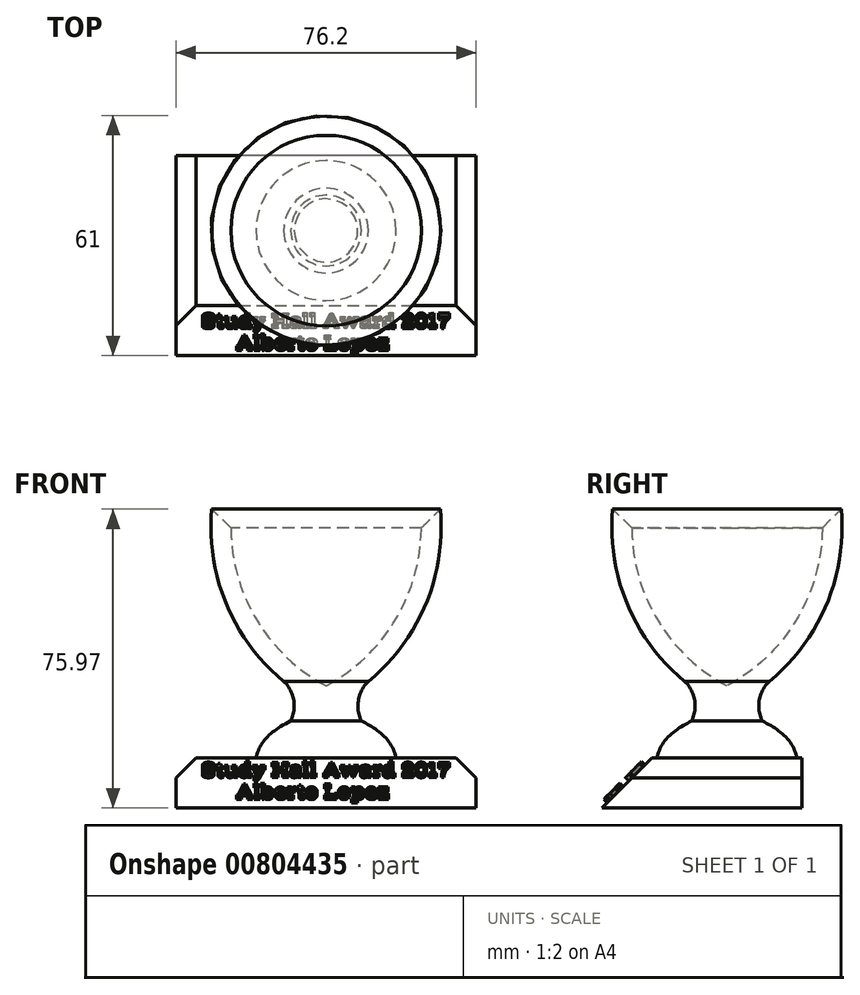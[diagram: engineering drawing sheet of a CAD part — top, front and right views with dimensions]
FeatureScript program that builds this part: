
annotation { "Feature Type Name" : "Feature", "Feature Type Description" : "" }
export const myFeature = defineFeature(function(context is Context, id is Id, definition is map)
    precondition{}
    {
        {
            var Q0;
            Q0=qCreatedBy(makeId("Top.planeOp"),FACE);
            var sketch = newSketch(context, id + "F0", { "sketchPlane" : qUnion([Q0])});
            skLineSegment(sketch, "E0.bottom", {"start": v(38.1, 25.4) * mm, "end": v(-38.1, 25.4) * mm});
            skLineSegment(sketch, "E0.top", {"start": v(38.1, -25.4) * mm, "end": v(-38.1, -25.4) * mm});
            skLineSegment(sketch, "E0.left", {"start": v(38.1, 25.4) * mm, "end": v(38.1, -25.4) * mm});
            skLineSegment(sketch, "E0.right", {"start": v(-38.1, 25.4) * mm, "end": v(-38.1, -25.4) * mm});
            skPoint(sketch, "E0.middle", {"position": v(0, 0) * mm});
            skSolve(sketch);
        }
        {
            var Q0;
            Q0=makeQuery(id+"F0.imprint","IMPRINT",FACE,{"disambiguationData":[TD([[makeQuery(id+"F0.imprint","IMPRINT",EDGE,{"derivedFrom":sQuery(id+"F0.wireOp",EDGE,"E0.bottom")}),1.0]])]});
            extrude(context, id + "F1", {"entities" : qUnion([Q0]), "depth" : 12.7 * mm, "offsetDistance" : 25.4 * mm});
        }
        {
            var Q0;
            Q0=makeQuery(id+"F1.opExtrude","CAP_EDGE",EDGE,{"disambiguationData":[OSD([sQuery(id+"F0.wireOp",EDGE,"E0.top")])],"isStart":false});
            chamfer(context, id + "F2", {"entities" : qUnion([Q0]), "width" : 12.7 * mm, "tangentPropagation" : true});
        }
        {
            var Q0;
            Q0=makeQuery(id+"F2.opChamfer","BLEND_FACE",FACE,{"disambiguationData":[OSD([sQuery(id+"F0.wireOp",EDGE,"E0.top")])]});
            var sketch = newSketch(context, id + "F3", { "sketchPlane" : qUnion([Q0])});
            skText(sketch, "E1", { "text": "Study Hall Award 2017\n      Alberto Lopez", "fontName": "RobotoSlab-Regular.ttf"});
            const initialGuessF3  = {"E1": [-0.03175, -0.007, 1, 0, 0.00428]};
            skSetInitialGuess(sketch, initialGuessF3);
            skSolve(sketch);
        }
        {
            var Q0;
            Q0=qSketchRegion(id+"F3",true);
            extrude(context, id + "F4", {"entities" : qUnion([Q0]), "operationType" : NewBodyOperationType.ADD, "depth" : 1.27 * mm, "offsetDistance" : 25.4 * mm});
        }
        {
            var Q0;
            Q0=qCreatedBy(makeId("Front.planeOp"),FACE);
            cPlane(context, id + "F5", {"entities" : qUnion([Q0]), "cplaneType" : CPlaneType.OFFSET, "offset" : 6.35 * mm, "oppositeDirection" : true, "width" : 152.4 * mm, "height" : 152.4 * mm});
        }
        {
            var Q0;
            Q0=qCreatedBy(id+"F5.planeOp",FACE);
            var sketch = newSketch(context, id + "F6", { "sketchPlane" : qUnion([Q0])});
            skLineSegment(sketch, "E2", {"start": v(0, 0) * mm, "end": v(0, 76.2) * mm});
            skLineSegment(sketch, "E3", {"start": v(0, 76.2) * mm, "end": v(29.02, 76.2) * mm});
            skArc(sketch, "E4", {"start": v(0, 25.4) * mm, "mid": v(22.56, 46.2) * mm, "end": v(29.02, 76.2) * mm});
            skLineSegment(sketch, "E5.0.1", {"start": v(-38.1, 12.7) * mm, "end": v(38.1, 12.7) * mm});
            skLineSegment(sketch, "E5.0.3", {"start": v(38.1, 12.7) * mm, "end": v(-38.1, 12.7) * mm});
            skLineSegment(sketch, "E6.bottom", {"start": v(0, 25.4) * mm, "end": v(17.78, 25.4) * mm});
            skLineSegment(sketch, "E6.top", {"start": v(0, 12.7) * mm, "end": v(17.78, 12.7) * mm});
            skLineSegment(sketch, "E6.left", {"start": v(0, 25.4) * mm, "end": v(0, 12.7) * mm});
            skLineSegment(sketch, "E6.right", {"start": v(17.78, 25.4) * mm, "end": v(17.78, 12.7) * mm});
            skFitSpline(sketch, "E7", {"points": [v(0, 25.4) * mm, v(17.78, 12.7) * mm, v(16.67, -4.04) * mm, v(20.3, -14.25) * mm], "startDerivative": vector(88.16, -26.05) * mm, "endDerivative": vector(28.03, -36.89) * mm});
            skArc(sketch, "E8", {"start": v(10.75, 32.19) * mm, "mid": v(8.22, 27.43) * mm, "end": v(8.98, 22.1) * mm});
            skArc(sketch, "E9", {"start": v(0, 31.05) * mm, "mid": v(18.87, 49.97) * mm, "end": v(23.94, 76.2) * mm});
            skSolve(sketch);
        }
        {
            var Q0;
            {var subQ1=sQuery(id+"F6.wireOp",EDGE,"E6.bottom");var subQ3=sQuery(id+"F6.wireOp",EDGE,"E8");var subQ4=makeQuery(id+"F6.imprint","INTERSECT",VERTEX,{"derivedFrom":[subQ1,subQ3]});Q0=makeQuery(id+"F6.imprint","IMPRINT",FACE,{"disambiguationData":[TD([[makeQuery(id+"F6.imprint","IMPRINT",EDGE,{"disambiguationData":[TD([[subQ4,-1.0]])],"derivedFrom":subQ3}),-1.0]])]});}
            var Q1;
            {var subQ0=sQuery(id+"F6.wireOp",EDGE,"E6.bottom");var subQ3=sQuery(id+"F6.wireOp",EDGE,"E8");var subQ5=makeQuery(id+"F6.imprint","INTERSECT",VERTEX,{"derivedFrom":[subQ0,subQ3]});Q1=makeQuery(id+"F6.imprint","IMPRINT",FACE,{"disambiguationData":[TD([[makeQuery(id+"F6.imprint","IMPRINT",EDGE,{"disambiguationData":[TD([[subQ5,1.0]])],"derivedFrom":subQ3}),-1.0]])]});}
            var Q2;
            {var subQ1=sQuery(id+"F6.wireOp",EDGE,"E2");var subQ3=sQuery(id+"F6.wireOp",EDGE,"E5.0.1");var subQ4=makeQuery(id+"F6.imprint","INTERSECT",VERTEX,{"derivedFrom":[subQ1,subQ3]});Q2=makeQuery(id+"F6.imprint","IMPRINT",FACE,{"disambiguationData":[TD([[makeQuery(id+"F6.imprint","IMPRINT",EDGE,{"disambiguationData":[TD([[subQ4,-1.0]])],"derivedFrom":subQ3}),1.0]])]});}
            var Q3;
            {var subQ6=sQuery(id+"F6.wireOp",EDGE,"E9");Q3=makeQuery(id+"F6.imprint","IMPRINT",FACE,{"disambiguationData":[TD([[makeQuery(id+"F6.imprint","IMPRINT",EDGE,{"derivedFrom":subQ6}),-1.0]])]});}
            var Q4;
            Q4=sQuery(id+"F6.wireOp",EDGE,"E2");
            revolve(context, id + "F7", {"operationType" : NewBodyOperationType.ADD, "surfaceOperationType" : NewSurfaceOperationType.NEW, "entities" : qUnion([Q0, Q1, Q2, Q3]), "axis" : qUnion([Q4]), "revolveType" : RevolveType.FULL});
        }
        {
            var Q0;
            Q0=makeQuery(id+"F1.opExtrude","CAP_EDGE",EDGE,{"disambiguationData":[OSD([sQuery(id+"F0.wireOp",EDGE,"E0.right")])],"isStart":false});
            var Q1;
            Q1=makeQuery(id+"F1.opExtrude","CAP_EDGE",EDGE,{"disambiguationData":[OSD([sQuery(id+"F0.wireOp",EDGE,"E0.left")])],"isStart":false});
            chamfer(context, id + "F8", {"entities" : qUnion([Q0, Q1]), "width" : 5.08 * mm, "tangentPropagation" : true});
        }
        {
            var Q0;
            Q0=makeQuery(id+"F7.opRevolve","SWEPT_EDGE",EDGE,{"disambiguationData":[OSD([sQuery(id+"F6.wireOp",EDGE,"E3"),sQuery(id+"F6.wireOp",EDGE,"E9")])]});
            chamfer(context, id + "F9", {"entities" : qUnion([Q0]), "width" : 5.08 * mm, "tangentPropagation" : true});
        }
    });
